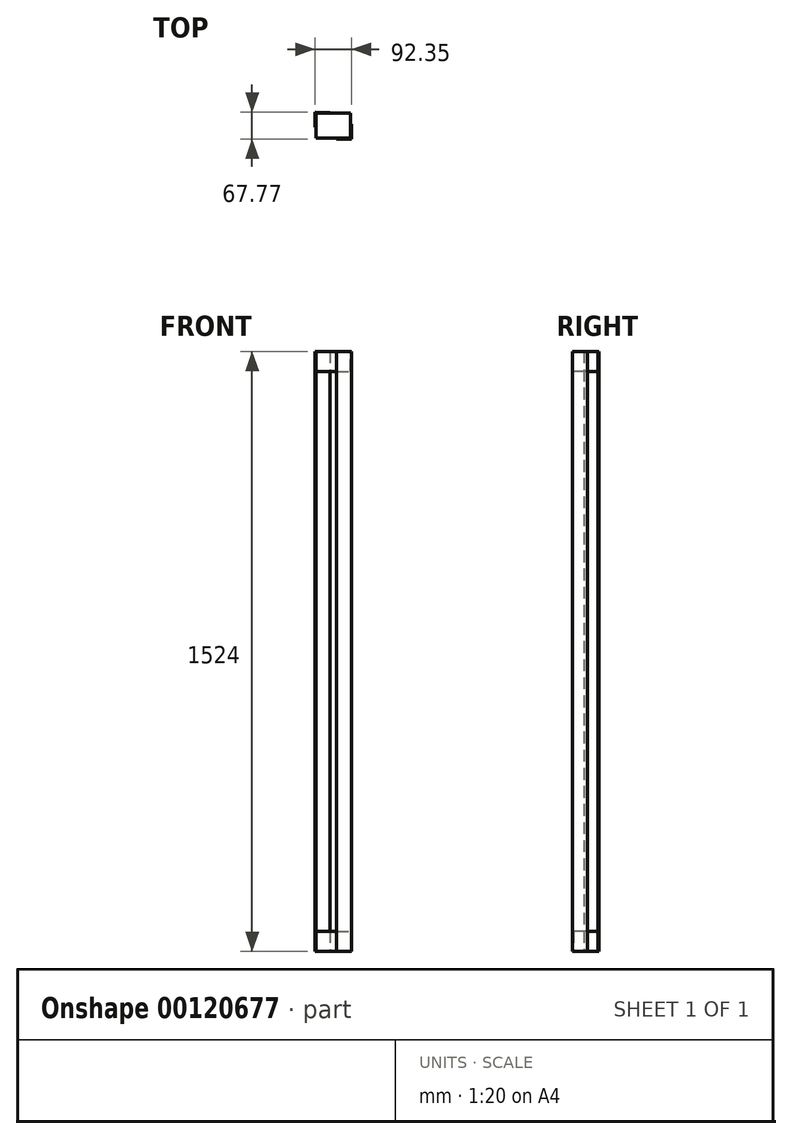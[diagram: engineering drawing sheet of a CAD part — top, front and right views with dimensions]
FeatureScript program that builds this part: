
annotation { "Feature Type Name" : "Feature", "Feature Type Description" : "" }
export const myFeature = defineFeature(function(context is Context, id is Id, definition is map)
    precondition{}
    {
        {
            var Q0;
            Q0=qCreatedBy(makeId("Top.planeOp"),FACE);
            var sketch = newSketch(context, id + "F0", { "sketchPlane" : qUnion([Q0])});
            skLineSegment(sketch, "E0", {"start": v(0, 67.77) * mm, "end": v(38.1, 67.46) * mm});
            skLineSegment(sketch, "E1", {"start": v(54.25, 0) * mm, "end": v(92.35, 0) * mm});
            skLineSegment(sketch, "E2", {"start": v(92.35, 0) * mm, "end": v(92.35, 38.1) * mm});
            skLineSegment(sketch, "E3", {"start": v(38.1, 67.46) * mm, "end": v(38.1, 65.48) * mm});
            skLineSegment(sketch, "E4", {"start": v(38.1, 65.48) * mm, "end": v(1.98, 65.48) * mm});
            skLineSegment(sketch, "E5", {"start": v(1.98, 29.67) * mm, "end": v(0, 29.67) * mm});
            skLineSegment(sketch, "E6", {"start": v(92.35, 38.1) * mm, "end": v(90.37, 38.1) * mm});
            skLineSegment(sketch, "E7", {"start": v(90.37, 38.1) * mm, "end": v(90.37, 1.98) * mm});
            skLineSegment(sketch, "E8", {"start": v(90.37, 1.98) * mm, "end": v(54.25, 1.98) * mm});
            skLineSegment(sketch, "E9", {"start": v(54.25, 1.98) * mm, "end": v(54.25, 0) * mm});
            skLineSegment(sketch, "E10", {"start": v(0, 67.77) * mm, "end": v(0, 29.67) * mm});
            skLineSegment(sketch, "E11", {"start": v(1.98, 65.48) * mm, "end": v(1.98, 29.67) * mm});
            skLineSegment(sketch, "E12.bottom", {"start": v(2.24, 65.26) * mm, "end": v(90.2, 65.26) * mm});
            skLineSegment(sketch, "E12.top", {"start": v(2.24, 2.14) * mm, "end": v(90.2, 2.14) * mm});
            skLineSegment(sketch, "E12.left", {"start": v(2.24, 65.26) * mm, "end": v(2.24, 2.14) * mm});
            skLineSegment(sketch, "E12.right", {"start": v(90.2, 65.26) * mm, "end": v(90.2, 2.14) * mm});
            skSolve(sketch);
        }
        {
            var Q0;
            Q0=makeQuery(id+"F0.imprint","IMPRINT",FACE,{"disambiguationData":[TD([[makeQuery(id+"F0.imprint","IMPRINT",EDGE,{"derivedFrom":sQuery(id+"F0.wireOp",EDGE,"E0")}),-1.0]])]});
            var Q1;
            Q1=makeQuery(id+"F0.imprint","IMPRINT",FACE,{"disambiguationData":[TD([[makeQuery(id+"F0.imprint","IMPRINT",EDGE,{"derivedFrom":sQuery(id+"F0.wireOp",EDGE,"E1")}),1.0]])]});
            extrude(context, id + "F1", {"entities" : qUnion([Q0, Q1]), "depth" : 1524 * mm});
        }
        {
            var Q0;
            Q0=makeQuery(id+"F0.imprint","IMPRINT",FACE,{"disambiguationData":[TD([[makeQuery(id+"F0.imprint","IMPRINT",EDGE,{"derivedFrom":sQuery(id+"F0.wireOp",EDGE,"E12.bottom")}),-1.0]])]});
            extrude(context, id + "F2", {"entities" : qUnion([Q0]), "depth" : 50.8 * mm});
        }
        {
            var Q0;
            Q0=makeQuery(id+"F1.opExtrude","CAP_FACE",FACE,{"disambiguationData":[OSD([sQuery(id+"F0.wireOp",EDGE,"E0"),sQuery(id+"F0.wireOp",EDGE,"E3"),sQuery(id+"F0.wireOp",EDGE,"E4"),sQuery(id+"F0.wireOp",EDGE,"E5"),sQuery(id+"F0.wireOp",EDGE,"E10"),sQuery(id+"F0.wireOp",EDGE,"E11")])],"isStart":false});
            var sketch = newSketch(context, id + "F3", { "sketchPlane" : qUnion([Q0])});
            skLineSegment(sketch, "E13.bottom", {"start": v(2.13, 65.33) * mm, "end": v(90.17, 65.33) * mm});
            skLineSegment(sketch, "E13.top", {"start": v(2.13, 2.15) * mm, "end": v(90.17, 2.15) * mm});
            skLineSegment(sketch, "E13.left", {"start": v(2.13, 65.33) * mm, "end": v(2.13, 2.15) * mm});
            skLineSegment(sketch, "E13.right", {"start": v(90.17, 65.33) * mm, "end": v(90.17, 2.15) * mm});
            skSolve(sketch);
        }
        {
            var Q0;
            Q0 = qSketchRegion(id + "F3", true);
            extrude(context, id + "F4", {"entities" : qUnion([Q0]), "oppositeDirection" : true, "depth" : 50.8 * mm});
        }
    });
